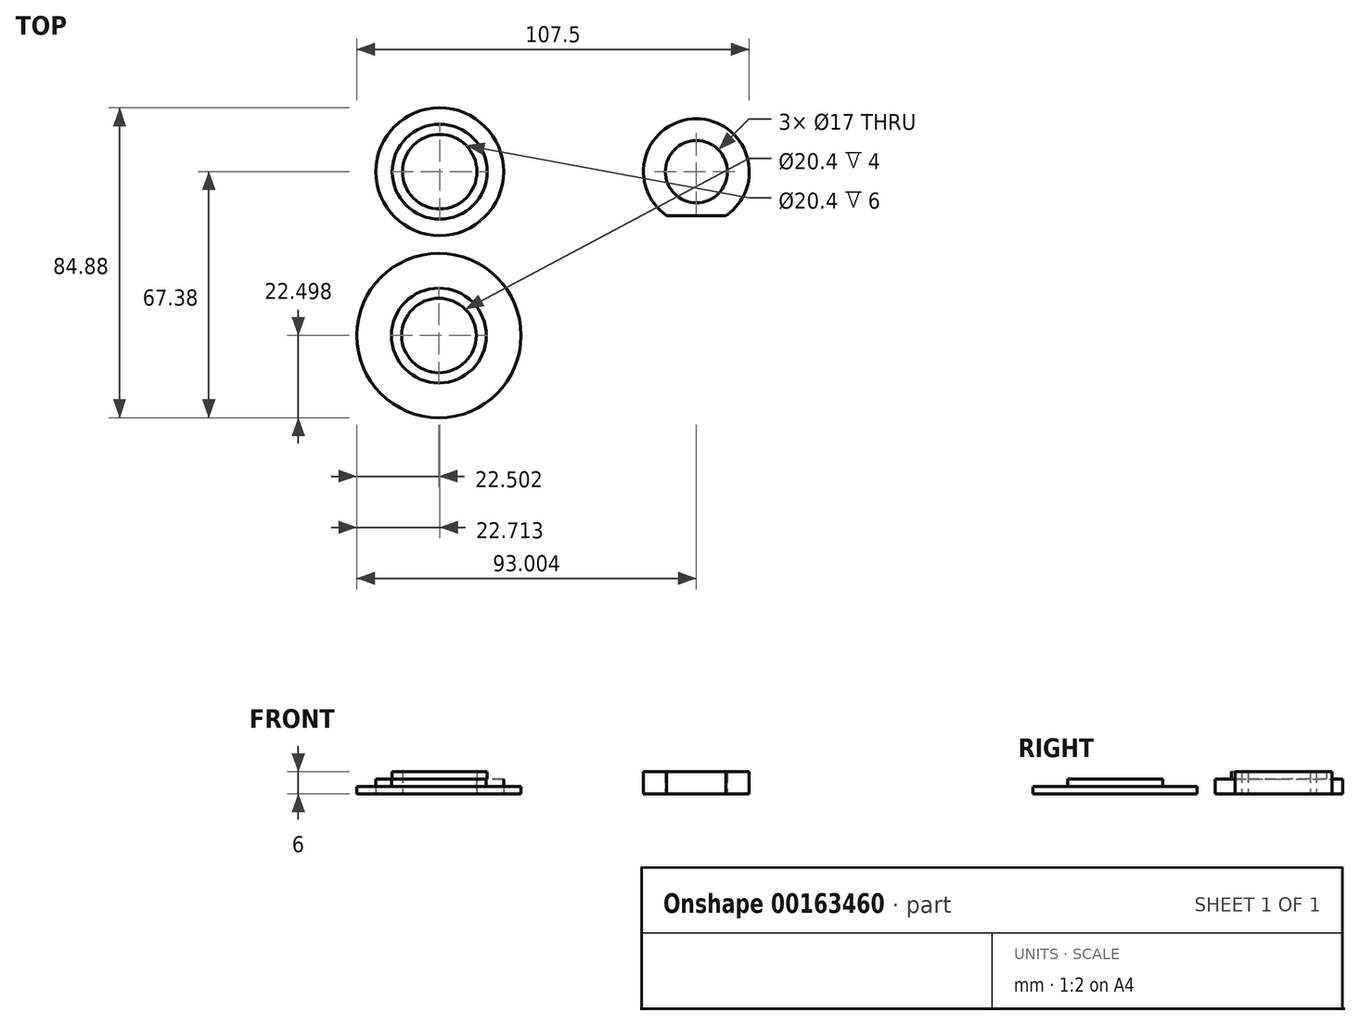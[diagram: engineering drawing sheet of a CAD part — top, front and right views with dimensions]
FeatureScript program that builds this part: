
annotation { "Feature Type Name" : "Feature", "Feature Type Description" : "" }
export const myFeature = defineFeature(function(context is Context, id is Id, definition is map)
    precondition{}
    {
        {
            var Q0;
            Q0=qCreatedBy(makeId("Top.planeOp"),FACE);
            var sketch = newSketch(context, id + "F0", { "sketchPlane" : qUnion([Q0]), "disableImprinting" : false});
            skCircle(sketch, "E0", {"center": v(-42.85, 0) * mm, "radius": 17.5 * mm});
            skCircle(sketch, "E1", {"center": v(-42.85, 0) * mm, "radius": 10.2 * mm});
            skSolve(sketch);
        }
        {
            var Q0;
            Q0=makeQuery(id+"F0.imprint","IMPRINT",FACE,{"disambiguationData":[TD([[makeQuery(id+"F0.imprint","IMPRINT",EDGE,{"derivedFrom":sQuery(id+"F0.wireOp",EDGE,"E0")}),1.0]])]});
            extrude(context, id + "F1", {"entities" : qUnion([Q0]), "depth" : 4 * mm, "offsetDistance" : 25 * mm});
        }
        {
            var Q0;
            Q0=makeQuery(id+"F1.opExtrude","CAP_FACE",FACE,{"disambiguationData":[OSD([sQuery(id+"F0.wireOp",EDGE,"E0"),sQuery(id+"F0.wireOp",EDGE,"E1")])],"isStart":false});
            var sketch = newSketch(context, id + "F2", { "sketchPlane" : qUnion([Q0]), "disableImprinting" : false});
            skCircle(sketch, "E2.0", {"center": v(-42.85, 0) * mm, "radius": 10.2 * mm});
            skCircle(sketch, "E3", {"center": v(-42.85, 0) * mm, "radius": 13 * mm});
            skSolve(sketch);
        }
        {
            var Q0;
            Q0=makeQuery(id+"F2.imprint","IMPRINT",FACE,{"disambiguationData":[TD([[makeQuery(id+"F2.imprint","IMPRINT",EDGE,{"derivedFrom":sQuery(id+"F2.wireOp",EDGE,"E2.0")}),-1.0]])]});
            extrude(context, id + "F3", {"entities" : qUnion([Q0]), "operationType" : NewBodyOperationType.ADD, "depth" : 2 * mm, "offsetDistance" : 25 * mm});
        }
        {
            var Q0;
            Q0=qCreatedBy(makeId("Top.planeOp"),FACE);
            var sketch = newSketch(context, id + "F4", { "sketchPlane" : qUnion([Q0])});
            skCircle(sketch, "E4", {"center": v(27.44, 0) * mm, "radius": 8.5 * mm});
            skArc(sketch, "E5", {"start": v(35.58, -12) * mm, "mid": v(27.44, 14.5) * mm, "end": v(19.3, -12) * mm});
            skLineSegment(sketch, "E6", {"start": v(19.3, -12) * mm, "end": v(35.58, -12) * mm});
            skSolve(sketch);
        }
        {
            var Q0;
            Q0=makeQuery(id+"F4.imprint","IMPRINT",FACE,{"disambiguationData":[TD([[makeQuery(id+"F4.imprint","IMPRINT",EDGE,{"derivedFrom":sQuery(id+"F4.wireOp",EDGE,"E4")}),-1.0]])]});
            extrude(context, id + "F5", {"entities" : qUnion([Q0]), "depth" : 6 * mm, "offsetDistance" : 25 * mm});
        }
        {
            var Q0;
            Q0=qCreatedBy(makeId("Top.planeOp"),FACE);
            var sketch = newSketch(context, id + "F6", { "sketchPlane" : qUnion([Q0]), "disableImprinting" : false});
            skCircle(sketch, "E7", {"center": v(-43.06, -44.88) * mm, "radius": 22.5 * mm});
            skCircle(sketch, "E8", {"center": v(-43.06, -44.88) * mm, "radius": 10.2 * mm});
            skSolve(sketch);
        }
        {
            var Q0;
            Q0=makeQuery(id+"F6.imprint","IMPRINT",FACE,{"disambiguationData":[TD([[makeQuery(id+"F6.imprint","IMPRINT",EDGE,{"derivedFrom":sQuery(id+"F6.wireOp",EDGE,"E7")}),1.0]])]});
            extrude(context, id + "F7", {"entities" : qUnion([Q0]), "depth" : 2 * mm, "offsetDistance" : 25 * mm});
        }
        {
            var Q0;
            Q0=makeQuery(id+"F7.opExtrude","CAP_FACE",FACE,{"disambiguationData":[OSD([sQuery(id+"F6.wireOp",EDGE,"E7"),sQuery(id+"F6.wireOp",EDGE,"E8")])],"isStart":false});
            var sketch = newSketch(context, id + "F8", { "sketchPlane" : qUnion([Q0])});
            skCircle(sketch, "E9.0", {"center": v(-43.06, -44.88) * mm, "radius": 10.2 * mm});
            skCircle(sketch, "E10", {"center": v(-43.06, -44.88) * mm, "radius": 13 * mm});
            skSolve(sketch);
        }
        {
            var Q0;
            Q0 = qSketchRegion(id + "F8", true);
            extrude(context, id + "F9", {"entities" : qUnion([Q0]), "operationType" : NewBodyOperationType.ADD, "depth" : 2 * mm, "offsetDistance" : 25 * mm});
        }
    });
